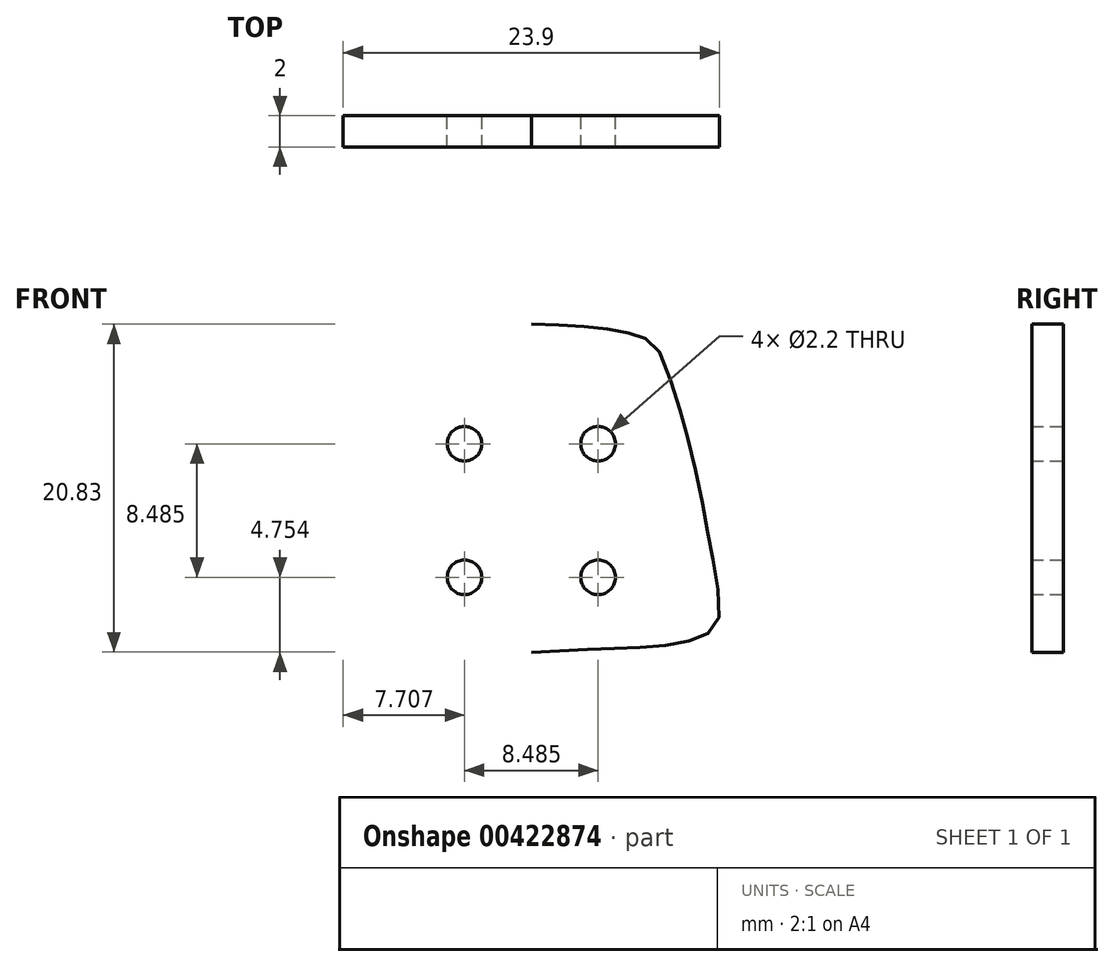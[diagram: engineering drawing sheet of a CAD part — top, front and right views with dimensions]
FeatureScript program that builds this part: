
annotation { "Feature Type Name" : "Feature", "Feature Type Description" : "" }
export const myFeature = defineFeature(function(context is Context, id is Id, definition is map)
    precondition{}
    {
        {
            var Q0;
            Q0=qCreatedBy(makeId("Front.planeOp"),FACE);
            var sketch = newSketch(context, id + "F0", { "sketchPlane" : qUnion([Q0])});
            skCircle(sketch, "E0", {"center": v(4.24, -5.22) * mm, "radius": 1.1 * mm});
            skCircle(sketch, "E1", {"center": v(-4.24, -5.22) * mm, "radius": 1.1 * mm});
            skCircle(sketch, "E2", {"center": v(-4.24, 3.27) * mm, "radius": 1.1 * mm});
            skCircle(sketch, "E3", {"center": v(4.24, 3.27) * mm, "radius": 1.1 * mm});
            skLineSegment(sketch, "E4", {"start": v(-11.8, -5.6) * mm, "end": v(-10.76, 0.08) * mm});
            skFitSpline(sketch, "E5", {"points": [v(0, 10.86) * mm, v(-2.43, 10.76) * mm, v(-4.46, 10.6) * mm, v(-6, 10.33) * mm, v(-7.12, 10) * mm, v(-7.97, 9.38) * mm, v(-9.15, 6.4) * mm, v(-9.87, 3.87) * mm, v(-10.76, 0.08) * mm, v(-11.29, -2.76) * mm, v(-11.8, -5.6) * mm, v(-11.8, -8.12) * mm, v(-10.95, -8.93) * mm, v(-9.5, -9.39) * mm, v(-7.34, -9.66) * mm, v(-5.18, -9.75) * mm, v(-2.65, -9.84) * mm, v(0, -9.97) * mm], "startDerivative": vector(-46.58, 0.42) * mm, "endDerivative": vector(41.02, -2.27) * mm});
            skFitSpline(sketch, "E6.MirrorCS", {"points": [v(0, 10.86) * mm, v(2.43, 10.76) * mm, v(4.46, 10.6) * mm, v(6, 10.33) * mm, v(7.12, 10) * mm, v(7.97, 9.38) * mm, v(9.15, 6.4) * mm, v(9.87, 3.87) * mm, v(10.76, 0.08) * mm, v(11.29, -2.76) * mm, v(11.8, -5.6) * mm, v(11.8, -8.12) * mm, v(10.95, -8.93) * mm, v(9.5, -9.39) * mm, v(7.34, -9.66) * mm, v(5.18, -9.75) * mm, v(2.65, -9.84) * mm, v(0, -9.97) * mm], "startDerivative": vector(46.58, 0.42) * mm, "endDerivative": vector(-41.02, -2.27) * mm});
            skSolve(sketch);
        }
        {
            var Q0;
            Q0=sQuery(id+"F0.wireOp",EDGE,"E3");
            var Q1;
            Q1=sQuery(id+"F0.wireOp",EDGE,"E2");
            var Q2;
            Q2=sQuery(id+"F0.wireOp",EDGE,"E1");
            var Q3;
            Q3=sQuery(id+"F0.wireOp",EDGE,"E0");
            var Q4;
            Q4=sQuery(id+"F0.wireOp",EDGE,"E6.MirrorCS");
            var Q5;
            Q5=sQuery(id+"F0.wireOp",EDGE,"E5");
            extrude(context, id + "F1", {"bodyType" : ToolBodyType.SURFACE, "surfaceEntities" : qUnion([Q0, Q1, Q2, Q3, Q4, Q5]), "oppositeDirection" : true, "depth" : 2 * mm});
        }
    });
